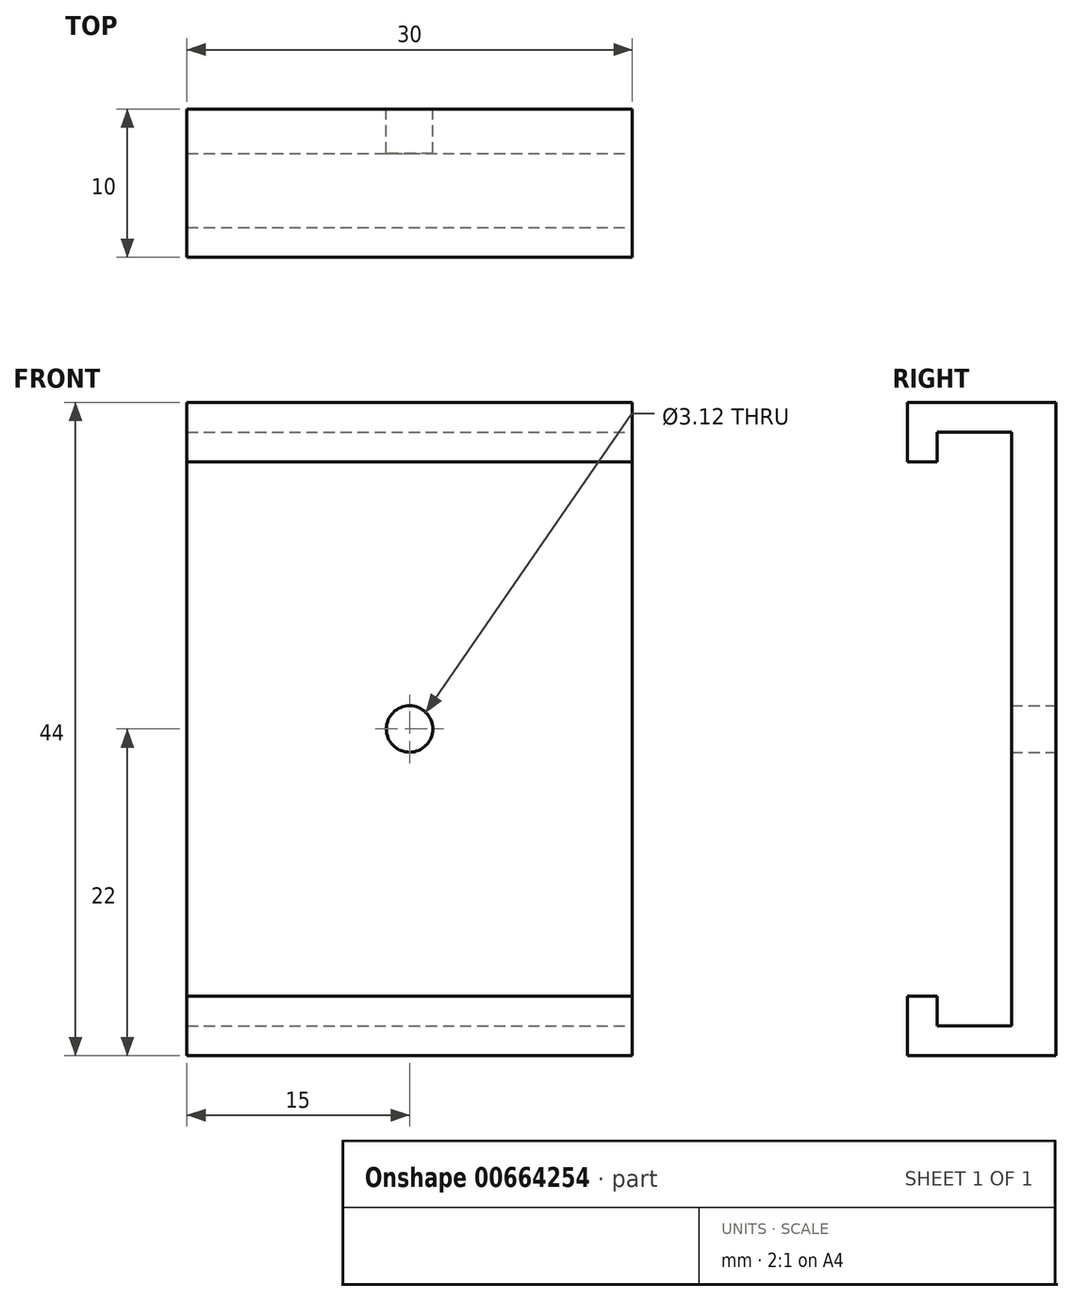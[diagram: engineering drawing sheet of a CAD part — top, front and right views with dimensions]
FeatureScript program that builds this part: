
annotation { "Feature Type Name" : "Feature", "Feature Type Description" : "" }
export const myFeature = defineFeature(function(context is Context, id is Id, definition is map)
    precondition{}
    {
        {
            var Q0;
            Q0=qCreatedBy(makeId("Front.planeOp"),FACE);
            var sketch = newSketch(context, id + "F0", { "sketchPlane" : qUnion([Q0])});
            skLineSegment(sketch, "E0.bottom", {"start": v(15, 22) * mm, "end": v(-15, 22) * mm});
            skLineSegment(sketch, "E0.top", {"start": v(15, -22) * mm, "end": v(-15, -22) * mm});
            skLineSegment(sketch, "E0.left", {"start": v(15, 22) * mm, "end": v(15, -22) * mm});
            skLineSegment(sketch, "E0.right", {"start": v(-15, 22) * mm, "end": v(-15, -22) * mm});
            skPoint(sketch, "E0.middle", {"position": v(0, 0) * mm});
            skCircle(sketch, "E1", {"center": v(0, 0) * mm, "radius": 1.56 * mm});
            skSolve(sketch);
        }
        {
            var Q0;
            Q0=makeQuery(id+"F0.imprint","IMPRINT",FACE,{"disambiguationData":[TD([[makeQuery(id+"F0.imprint","IMPRINT",EDGE,{"derivedFrom":sQuery(id+"F0.wireOp",EDGE,"E0.bottom")}),1.0]])]});
            extrude(context, id + "F1", {"entities" : qUnion([Q0]), "endBound" : BoundingType.SYMMETRIC, "depth" : 3 * mm, "offsetDistance" : 25 * mm});
        }
        {
            var Q0;
            Q0=makeQuery(id+"F1.opExtrude","CAP_FACE",FACE,{"disambiguationData":[OSD([sQuery(id+"F0.wireOp",EDGE,"E0.bottom"),sQuery(id+"F0.wireOp",EDGE,"E0.top"),sQuery(id+"F0.wireOp",EDGE,"E0.left"),sQuery(id+"F0.wireOp",EDGE,"E0.right"),sQuery(id+"F0.wireOp",EDGE,"E1")])],"isStart":false});
            var sketch = newSketch(context, id + "F2", { "sketchPlane" : qUnion([Q0])});
            skLineSegment(sketch, "E2.bottom", {"start": v(-15, 22) * mm, "end": v(15, 22) * mm});
            skLineSegment(sketch, "E2.top", {"start": v(-15, 20) * mm, "end": v(15, 20) * mm});
            skLineSegment(sketch, "E2.left", {"start": v(-15, 22) * mm, "end": v(-15, 20) * mm});
            skLineSegment(sketch, "E2.right", {"start": v(15, 22) * mm, "end": v(15, 20) * mm});
            skLineSegment(sketch, "E3.bottom", {"start": v(-15, -22) * mm, "end": v(15, -22) * mm});
            skLineSegment(sketch, "E3.top", {"start": v(-15, -20) * mm, "end": v(15, -20) * mm});
            skLineSegment(sketch, "E3.left", {"start": v(-15, -22) * mm, "end": v(-15, -20) * mm});
            skLineSegment(sketch, "E3.right", {"start": v(15, -22) * mm, "end": v(15, -20) * mm});
            skSolve(sketch);
        }
        {
            var Q0;
            Q0 = qSketchRegion(id + "F2", true);
            extrude(context, id + "F3", {"entities" : qUnion([Q0]), "operationType" : NewBodyOperationType.ADD, "depth" : 7 * mm, "offsetDistance" : 25 * mm});
        }
        {
            var Q0;
            Q0=makeQuery(id+"F3.opExtrude","SWEPT_FACE",FACE,{"disambiguationData":[OSD([sQuery(id+"F2.wireOp",EDGE,"E2.top")])]});
            var sketch = newSketch(context, id + "F4", { "sketchPlane" : qUnion([Q0])});
            skLineSegment(sketch, "E4.bottom", {"start": v(15, 8.5) * mm, "end": v(-15, 8.5) * mm});
            skLineSegment(sketch, "E4.top", {"start": v(15, 6.5) * mm, "end": v(-15, 6.5) * mm});
            skLineSegment(sketch, "E4.left", {"start": v(15, 8.5) * mm, "end": v(15, 6.5) * mm});
            skLineSegment(sketch, "E4.right", {"start": v(-15, 8.5) * mm, "end": v(-15, 6.5) * mm});
            skSolve(sketch);
        }
        {
            var Q0;
            Q0=makeQuery(id+"F4.imprint","IMPRINT",FACE,{"disambiguationData":[TD([[makeQuery(id+"F4.imprint","IMPRINT",EDGE,{"derivedFrom":sQuery(id+"F4.wireOp",EDGE,"E4.bottom")}),-1.0]])]});
            extrude(context, id + "F5", {"entities" : qUnion([Q0]), "operationType" : NewBodyOperationType.ADD, "depth" : 2 * mm, "offsetDistance" : 25 * mm});
        }
        {
            var Q0;
            Q0=makeQuery(id+"F3.opExtrude","SWEPT_FACE",FACE,{"disambiguationData":[OSD([sQuery(id+"F2.wireOp",EDGE,"E3.top")])]});
            var sketch = newSketch(context, id + "F6", { "sketchPlane" : qUnion([Q0])});
            skLineSegment(sketch, "E5.bottom", {"start": v(-15, -8.5) * mm, "end": v(15, -8.5) * mm});
            skLineSegment(sketch, "E5.top", {"start": v(-15, -6.5) * mm, "end": v(15, -6.5) * mm});
            skLineSegment(sketch, "E5.left", {"start": v(-15, -8.5) * mm, "end": v(-15, -6.5) * mm});
            skLineSegment(sketch, "E5.right", {"start": v(15, -8.5) * mm, "end": v(15, -6.5) * mm});
            skSolve(sketch);
        }
        {
            var Q0;
            Q0=makeQuery(id+"F6.imprint","IMPRINT",FACE,{"disambiguationData":[TD([[makeQuery(id+"F6.imprint","IMPRINT",EDGE,{"derivedFrom":sQuery(id+"F6.wireOp",EDGE,"E5.bottom")}),1.0]])]});
            extrude(context, id + "F7", {"entities" : qUnion([Q0]), "operationType" : NewBodyOperationType.ADD, "depth" : 2 * mm, "offsetDistance" : 25 * mm});
        }
    });
